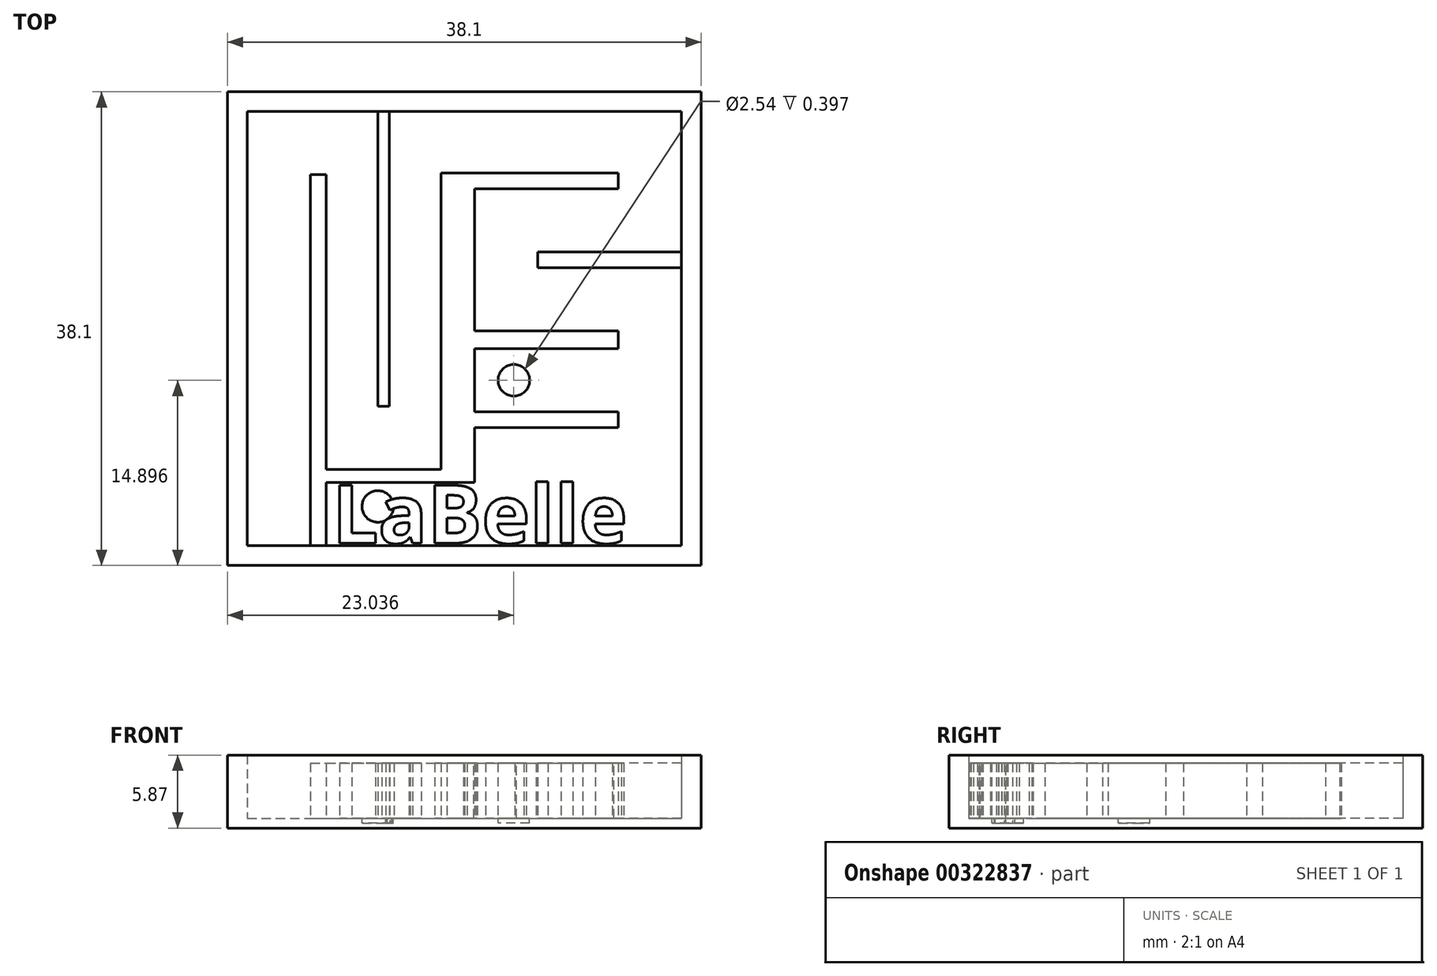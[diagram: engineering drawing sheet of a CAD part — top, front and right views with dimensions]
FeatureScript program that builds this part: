
annotation { "Feature Type Name" : "Feature", "Feature Type Description" : "" }
export const myFeature = defineFeature(function(context is Context, id is Id, definition is map)
    precondition{}
    {
        {
            var Q0;
            Q0=qCreatedBy(makeId("Top.planeOp"),FACE);
            var sketch = newSketch(context, id + "F0", { "sketchPlane" : qUnion([Q0])});
            skLineSegment(sketch, "E0.bottom", {"start": v(-17.2, 16.67) * mm, "end": v(20.9, 16.67) * mm});
            skLineSegment(sketch, "E0.top", {"start": v(-17.2, -21.43) * mm, "end": v(20.9, -21.43) * mm});
            skLineSegment(sketch, "E0.left", {"start": v(-17.2, 16.67) * mm, "end": v(-17.2, -21.43) * mm});
            skLineSegment(sketch, "E0.right", {"start": v(20.9, 16.67) * mm, "end": v(20.9, -21.43) * mm});
            skSolve(sketch);
        }
        {
            var Q0;
            Q0=makeQuery(id+"F0.imprint","IMPRINT",FACE,{"disambiguationData":[TD([[makeQuery(id+"F0.imprint","IMPRINT",EDGE,{"derivedFrom":sQuery(id+"F0.wireOp",EDGE,"E0.bottom")}),-1.0]])]});
            extrude(context, id + "F1", {"entities" : qUnion([Q0]), "depth" : 0.8 * mm});
        }
        {
            var Q0;
            Q0=makeQuery(id+"F1.opExtrude","CAP_FACE",FACE,{"disambiguationData":[OSD([sQuery(id+"F0.wireOp",EDGE,"E0.bottom"),sQuery(id+"F0.wireOp",EDGE,"E0.top"),sQuery(id+"F0.wireOp",EDGE,"E0.left"),sQuery(id+"F0.wireOp",EDGE,"E0.right")])],"isStart":false});
            var sketch = newSketch(context, id + "F2", { "sketchPlane" : qUnion([Q0])});
            skLineSegment(sketch, "E1.0", {"start": v(-15.6, 15.08) * mm, "end": v(19.32, 15.08) * mm});
            skLineSegment(sketch, "E1.1", {"start": v(-15.6, 15.08) * mm, "end": v(-15.6, -19.84) * mm});
            skLineSegment(sketch, "E1.2", {"start": v(-15.6, -19.84) * mm, "end": v(19.32, -19.84) * mm});
            skLineSegment(sketch, "E1.3", {"start": v(19.32, 15.08) * mm, "end": v(19.32, -19.84) * mm});
            skSolve(sketch);
        }
        {
            var Q0;
            Q0=makeQuery(id+"F2.imprint","IMPRINT",FACE,{"disambiguationData":[TD([[makeQuery(id+"F2.imprint","IMPRINT",EDGE,{"derivedFrom":sQuery(id+"F2.wireOp",EDGE,"E1.0")}),1.0]])]});
            extrude(context, id + "F3", {"entities" : qUnion([Q0]), "operationType" : NewBodyOperationType.ADD, "depth" : 5.08 * mm});
        }
        {
            var Q0;
            Q0=makeQuery(id+"F1.opExtrude","CAP_FACE",FACE,{"disambiguationData":[OSD([sQuery(id+"F0.wireOp",EDGE,"E0.bottom"),sQuery(id+"F0.wireOp",EDGE,"E0.top"),sQuery(id+"F0.wireOp",EDGE,"E0.left"),sQuery(id+"F0.wireOp",EDGE,"E0.right")])],"isStart":false});
            var sketch = newSketch(context, id + "F4", { "sketchPlane" : qUnion([Q0])});
            skLineSegment(sketch, "E2.bottom", {"start": v(-10.53, -19.84) * mm, "end": v(-9.26, -19.84) * mm});
            skLineSegment(sketch, "E2.top", {"start": v(-10.53, 10) * mm, "end": v(-9.26, 10) * mm});
            skLineSegment(sketch, "E2.left", {"start": v(-10.53, -19.84) * mm, "end": v(-10.53, 10) * mm});
            skLineSegment(sketch, "E2.right", {"start": v(-9.26, -19.84) * mm, "end": v(-9.26, -14.76) * mm});
            skLineSegment(sketch, "E3.bottom", {"start": v(-5.08, 15.08) * mm, "end": v(-4.18, 15.08) * mm});
            skLineSegment(sketch, "E3.top", {"start": v(-5.08, -8.62) * mm, "end": v(-4.18, -8.62) * mm});
            skLineSegment(sketch, "E3.left", {"start": v(-4.18, 15.08) * mm, "end": v(-4.18, -8.62) * mm});
            skLineSegment(sketch, "E3.right", {"start": v(-5.08, 15.08) * mm, "end": v(-5.08, -8.62) * mm});
            skLineSegment(sketch, "E4.top", {"start": v(-9.26, -14.76) * mm, "end": v(0, -14.76) * mm});
            skLineSegment(sketch, "E5.bottom", {"start": v(0, -14.76) * mm, "end": v(2.68, -14.76) * mm});
            skLineSegment(sketch, "E5.left", {"start": v(0, -13.7) * mm, "end": v(0, 10.07) * mm});
            skLineSegment(sketch, "E5.right", {"start": v(2.68, -14.76) * mm, "end": v(2.68, -10.34) * mm});
            skLineSegment(sketch, "E6.bottom", {"start": v(2.68, 8.87) * mm, "end": v(14.24, 8.87) * mm});
            skLineSegment(sketch, "E6.top", {"start": v(2.68, 10.14) * mm, "end": v(14.24, 10.14) * mm});
            skLineSegment(sketch, "E6.right", {"start": v(14.24, 8.87) * mm, "end": v(14.24, 10.14) * mm});
            skLineSegment(sketch, "E7.bottom", {"start": v(19.32, 2.52) * mm, "end": v(7.76, 2.52) * mm});
            skLineSegment(sketch, "E7.top", {"start": v(19.32, 3.79) * mm, "end": v(7.76, 3.79) * mm});
            skLineSegment(sketch, "E7.left", {"start": v(19.32, 2.52) * mm, "end": v(19.32, 3.79) * mm});
            skLineSegment(sketch, "E7.right", {"start": v(7.76, 2.52) * mm, "end": v(7.76, 3.79) * mm});
            skLineSegment(sketch, "E8.bottom", {"start": v(2.68, -4) * mm, "end": v(14.24, -4) * mm});
            skLineSegment(sketch, "E8.top", {"start": v(2.68, -2.56) * mm, "end": v(14.24, -2.56) * mm});
            skLineSegment(sketch, "E8.right", {"start": v(14.24, -4) * mm, "end": v(14.24, -2.56) * mm});
            skLineSegment(sketch, "E9.bottom", {"start": v(2.68, -10.34) * mm, "end": v(14.24, -10.34) * mm});
            skLineSegment(sketch, "E9.top", {"start": v(2.68, -9.07) * mm, "end": v(14.24, -9.07) * mm});
            skLineSegment(sketch, "E9.right", {"start": v(14.24, -10.34) * mm, "end": v(14.24, -9.07) * mm});
            skLineSegment(sketch, "E10", {"start": v(2.68, 10.14) * mm, "end": v(0, 10.14) * mm});
            skLineSegment(sketch, "E11", {"start": v(0, 10.14) * mm, "end": v(0, 10.07) * mm});
            skLineSegment(sketch, "E12.trimOffspring", {"start": v(2.68, -2.56) * mm, "end": v(2.68, 8.87) * mm});
            skLineSegment(sketch, "E13.trimOffspring", {"start": v(2.68, -9.07) * mm, "end": v(2.68, -4) * mm});
            skLineSegment(sketch, "E14.trimOffspring", {"start": v(-9.26, -13.7) * mm, "end": v(-9.26, 10) * mm});
            skLineSegment(sketch, "E15", {"start": v(-9.26, -13.7) * mm, "end": v(0, -13.7) * mm});
            skText(sketch, "E16", { "text": "LaBelle", "fontName": "OpenSans-Bold.ttf"});
            const initialGuessF4  = {"E16": [-0.00875, -0.01963, 1, 0, 0.0047]};
            skSetInitialGuess(sketch, initialGuessF4);
            skSolve(sketch);
        }
        {
            var Q0;
            Q0 = qSketchRegion(id + "F4", true);
            extrude(context, id + "F5", {"entities" : qUnion([Q0]), "operationType" : NewBodyOperationType.ADD, "depth" : 4.44 * mm});
        }
        {
            var Q0;
            Q0=makeQuery(id+"F5.boolean.opBoolean","SPLIT",FACE,{"disambiguationData":[TD([makeQuery(id+"F3.opExtrude","SWEPT_FACE",FACE,{"disambiguationData":[OSD([sQuery(id+"F2.wireOp",EDGE,"E1.0")])]})])],"derivedFrom":makeQuery(id+"F1.opExtrude","CAP_FACE",FACE,{"disambiguationData":[OSD([sQuery(id+"F0.wireOp",EDGE,"E0.bottom"),sQuery(id+"F0.wireOp",EDGE,"E0.top"),sQuery(id+"F0.wireOp",EDGE,"E0.left"),sQuery(id+"F0.wireOp",EDGE,"E0.right")])],"isStart":false})});
            var sketch = newSketch(context, id + "F6", { "sketchPlane" : qUnion([Q0])});
            skCircle(sketch, "E17", {"center": v(-5.1, -16.68) * mm, "radius": 1.27 * mm});
            skCircle(sketch, "E18", {"center": v(5.85, -6.53) * mm, "radius": 1.27 * mm});
            skPoint(sketch, "E18.centerSnap0", {"position": v(2.68, -6.53) * mm});
            skSolve(sketch);
        }
        {
            var Q0;
            Q0=makeQuery(id+"F6.imprint","IMPRINT",FACE,{"disambiguationData":[TD([[makeQuery(id+"F6.imprint","IMPRINT",EDGE,{"derivedFrom":sQuery(id+"F6.wireOp",EDGE,"E17")}),1.0]])]});
            var Q1;
            Q1=makeQuery(id+"F6.imprint","IMPRINT",FACE,{"disambiguationData":[TD([[makeQuery(id+"F6.imprint","IMPRINT",EDGE,{"derivedFrom":sQuery(id+"F6.wireOp",EDGE,"E18")}),1.0]])]});
            extrude(context, id + "F7", {"entities" : qUnion([Q0, Q1]), "operationType" : NewBodyOperationType.REMOVE, "oppositeDirection" : true, "depth" : 0.4 * mm});
        }
    });
